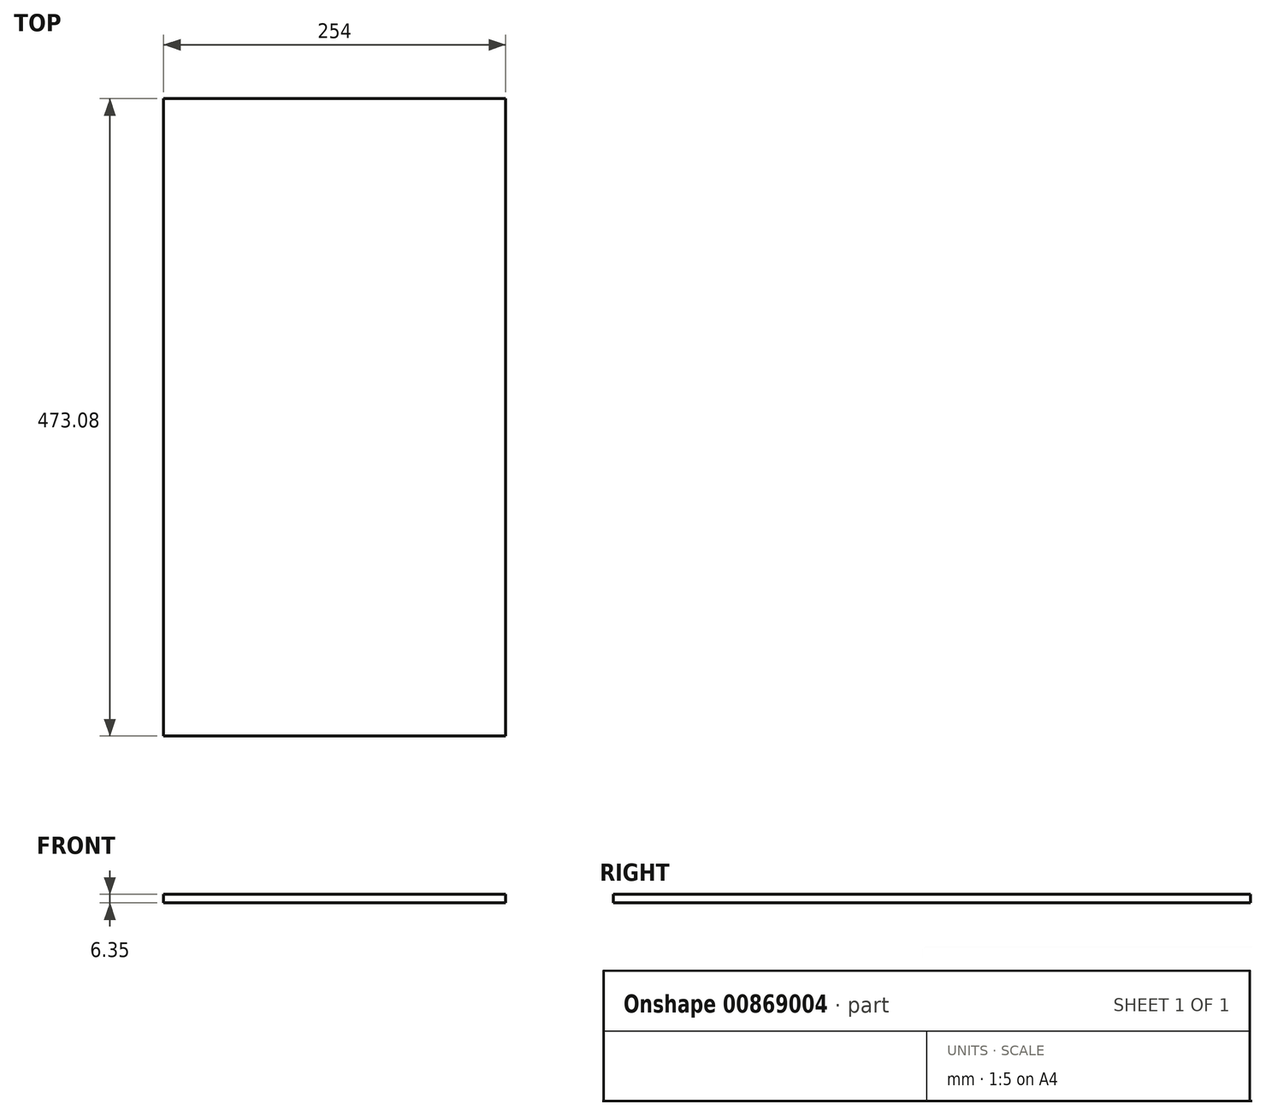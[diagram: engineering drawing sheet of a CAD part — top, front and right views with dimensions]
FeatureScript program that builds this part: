
annotation { "Feature Type Name" : "Feature", "Feature Type Description" : "" }
export const myFeature = defineFeature(function(context is Context, id is Id, definition is map)
    precondition{}
    {
        {
            var Q0;
            Q0=qCreatedBy(makeId("Top.planeOp"), FACE);
            var sketch = newSketch(context, id + "F0", { "sketchPlane" : qUnion([Q0]), "disableImprinting" : false});
            skLineSegment(sketch, "E0.bottom", {"start": v(-127, 236.54) * mm, "end": v(127, 236.54) * mm});
            skLineSegment(sketch, "E0.top", {"start": v(-127, -236.54) * mm, "end": v(127, -236.54) * mm});
            skLineSegment(sketch, "E0.left", {"start": v(-127, 236.54) * mm, "end": v(-127, -236.54) * mm});
            skLineSegment(sketch, "E0.right", {"start": v(127, 236.54) * mm, "end": v(127, -236.54) * mm});
            skPoint(sketch, "E0.middle", {"position": v(0, 0) * mm});
            skSolve(sketch);
        }
        {
            var Q0;
            Q0 = qSketchRegion(id + "F0", true);
            extrude(context, id + "F1", {"entities" : qUnion([Q0]), "depth" : 6.35 * mm, "offsetDistance" : 25.4 * mm});
        }
    });
